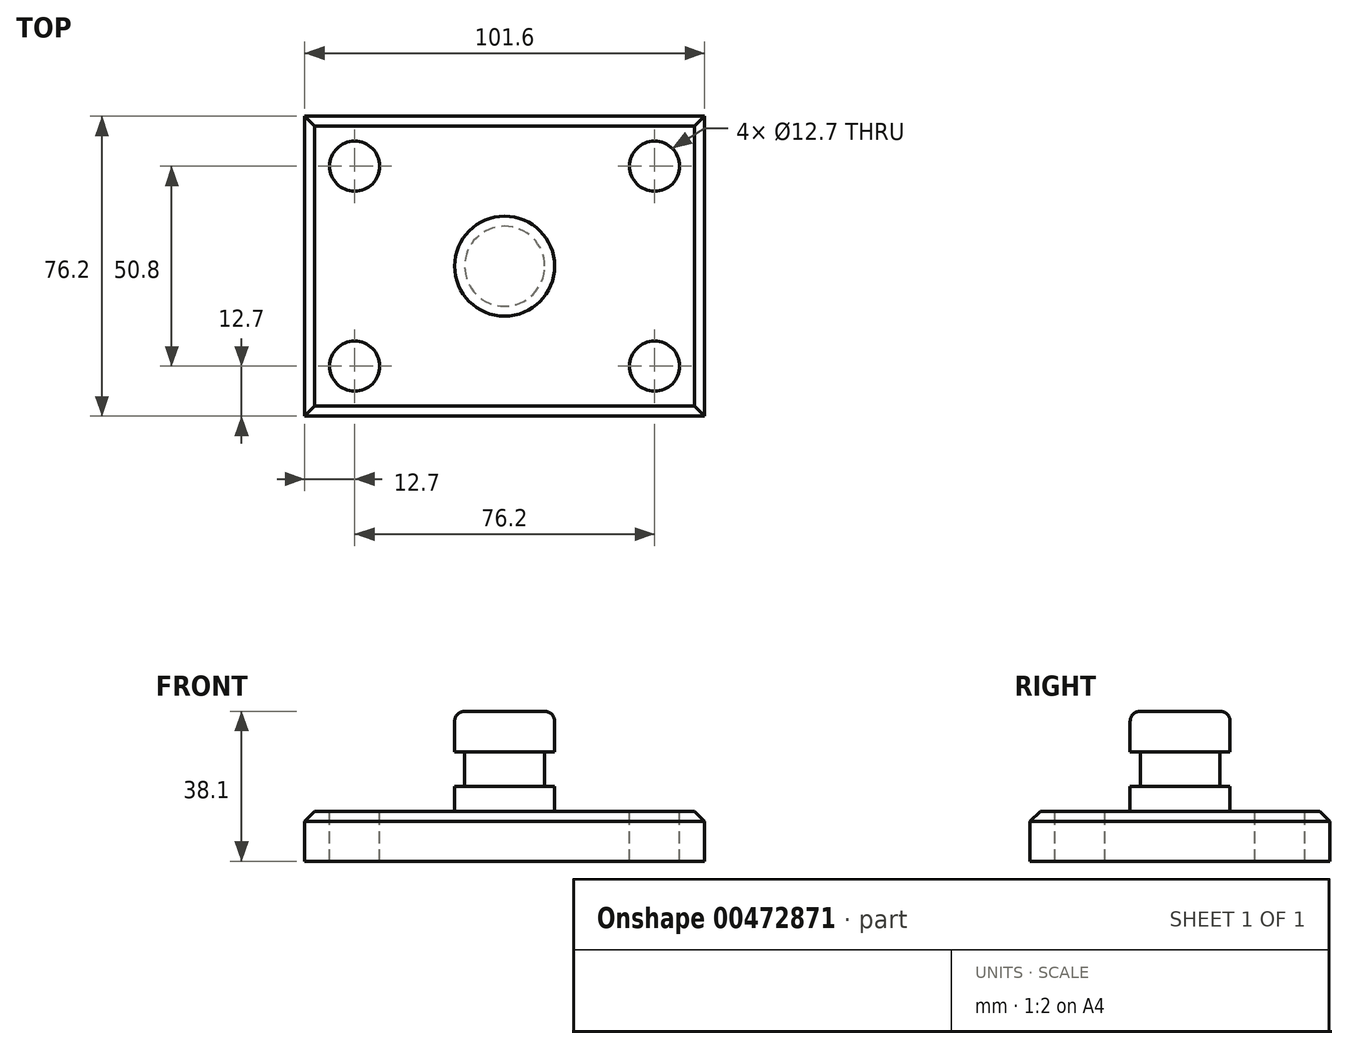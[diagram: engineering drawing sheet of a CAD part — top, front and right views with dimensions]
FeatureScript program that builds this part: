
annotation { "Feature Type Name" : "Feature", "Feature Type Description" : "" }
export const myFeature = defineFeature(function(context is Context, id is Id, definition is map)
    precondition{}
    {
        {
            var Q0;
            Q0=qCreatedBy(makeId("Top.planeOp"),FACE);
            var sketch = newSketch(context, id + "F0", { "sketchPlane" : qUnion([Q0])});
            skLineSegment(sketch, "E0.bottom", {"start": v(50.8, 38.1) * mm, "end": v(-50.8, 38.1) * mm});
            skLineSegment(sketch, "E0.top", {"start": v(50.8, -38.1) * mm, "end": v(-50.8, -38.1) * mm});
            skLineSegment(sketch, "E0.left", {"start": v(50.8, 38.1) * mm, "end": v(50.8, -38.1) * mm});
            skLineSegment(sketch, "E0.right", {"start": v(-50.8, 38.1) * mm, "end": v(-50.8, -38.1) * mm});
            skPoint(sketch, "E0.middle", {"position": v(0, 0) * mm});
            skSolve(sketch);
        }
        {
            var Q0;
            Q0=makeQuery(id+"F0.imprint","IMPRINT",FACE,{"disambiguationData":[TD([[makeQuery(id+"F0.imprint","IMPRINT",EDGE,{"derivedFrom":sQuery(id+"F0.wireOp",EDGE,"E0.bottom")}),1.0]])]});
            extrude(context, id + "F1", {"entities" : qUnion([Q0]), "depth" : 12.7 * mm});
        }
        {
            var Q0;
            Q0=makeQuery(id+"F1.opExtrude","CAP_FACE",FACE,{"disambiguationData":[OSD([sQuery(id+"F0.wireOp",EDGE,"E0.bottom"),sQuery(id+"F0.wireOp",EDGE,"E0.top"),sQuery(id+"F0.wireOp",EDGE,"E0.left"),sQuery(id+"F0.wireOp",EDGE,"E0.right")])],"isStart":false});
            var sketch = newSketch(context, id + "F2", { "sketchPlane" : qUnion([Q0])});
            skCircle(sketch, "E1", {"center": v(-38.1, 25.4) * mm, "radius": 6.35 * mm});
            skCircle(sketch, "E2", {"center": v(38.1, 25.4) * mm, "radius": 6.35 * mm});
            skCircle(sketch, "E3", {"center": v(-38.1, -25.4) * mm, "radius": 6.35 * mm});
            skCircle(sketch, "E4", {"center": v(38.1, -25.4) * mm, "radius": 6.35 * mm});
            skSolve(sketch);
        }
        {
            var Q0;
            Q0=makeQuery(id+"F2.imprint","IMPRINT",FACE,{"disambiguationData":[TD([[makeQuery(id+"F2.imprint","IMPRINT",EDGE,{"derivedFrom":sQuery(id+"F2.wireOp",EDGE,"E1")}),1.0]])]});
            var Q1;
            Q1=makeQuery(id+"F2.imprint","IMPRINT",FACE,{"disambiguationData":[TD([[makeQuery(id+"F2.imprint","IMPRINT",EDGE,{"derivedFrom":sQuery(id+"F2.wireOp",EDGE,"E2")}),1.0]])]});
            var Q2;
            Q2=makeQuery(id+"F2.imprint","IMPRINT",FACE,{"disambiguationData":[TD([[makeQuery(id+"F2.imprint","IMPRINT",EDGE,{"derivedFrom":sQuery(id+"F2.wireOp",EDGE,"E4")}),1.0]])]});
            var Q3;
            Q3=makeQuery(id+"F2.imprint","IMPRINT",FACE,{"disambiguationData":[TD([[makeQuery(id+"F2.imprint","IMPRINT",EDGE,{"derivedFrom":sQuery(id+"F2.wireOp",EDGE,"E3")}),1.0]])]});
            extrude(context, id + "F3", {"entities" : qUnion([Q0, Q1, Q2, Q3]), "operationType" : NewBodyOperationType.REMOVE, "endBound" : BoundingType.THROUGH_ALL, "oppositeDirection" : true, "depth" : 25.4 * mm});
        }
        {
            var Q0;
            Q0=qCreatedBy(makeId("Front.planeOp"),FACE);
            var sketch = newSketch(context, id + "F4", { "sketchPlane" : qUnion([Q0])});
            skLineSegment(sketch, "E5.bottom", {"start": v(0, 12.7) * mm, "end": v(12.7, 12.7) * mm});
            skLineSegment(sketch, "E5.top", {"start": v(0, 38.1) * mm, "end": v(12.7, 38.1) * mm});
            skLineSegment(sketch, "E5.left", {"start": v(0, 12.7) * mm, "end": v(0, 38.1) * mm});
            skLineSegment(sketch, "E5.right", {"start": v(12.7, 12.7) * mm, "end": v(12.7, 38.1) * mm});
            skSolve(sketch);
        }
        {
            var Q0;
            Q0=makeQuery(id+"F4.imprint","IMPRINT",FACE,{"disambiguationData":[TD([[makeQuery(id+"F4.imprint","IMPRINT",EDGE,{"derivedFrom":sQuery(id+"F4.wireOp",EDGE,"E5.bottom")}),1.0]])]});
            var Q1;
            Q1=sQuery(id+"F4.wireOp",EDGE,"E5.left");
            revolve(context, id + "F5", {"operationType" : NewBodyOperationType.ADD, "entities" : qUnion([Q0]), "axis" : qUnion([Q1]), "revolveType" : RevolveType.FULL});
        }
        {
            var Q0;
            Q0=qCreatedBy(makeId("Front.planeOp"),FACE);
            var sketch = newSketch(context, id + "F6", { "sketchPlane" : qUnion([Q0])});
            skLineSegment(sketch, "E6.bottom", {"start": v(10.16, 27.82) * mm, "end": v(18.9, 27.82) * mm});
            skLineSegment(sketch, "E6.top", {"start": v(10.16, 19.05) * mm, "end": v(18.9, 19.05) * mm});
            skLineSegment(sketch, "E6.left", {"start": v(10.16, 27.82) * mm, "end": v(10.16, 19.05) * mm});
            skLineSegment(sketch, "E6.right", {"start": v(18.9, 27.82) * mm, "end": v(18.9, 19.05) * mm});
            skSolve(sketch);
        }
        {
            var Q0;
            Q0=makeQuery(id+"F6.imprint","IMPRINT",FACE,{"disambiguationData":[TD([[makeQuery(id+"F6.imprint","IMPRINT",EDGE,{"derivedFrom":sQuery(id+"F6.wireOp",EDGE,"E6.bottom")}),-1.0]])]});
            var Q1;
            Q1=makeQuery(id+"F5.opRevolve","SWEPT_FACE",FACE,{"disambiguationData":[OSD([sQuery(id+"F4.wireOp",EDGE,"E5.right")])]});
            revolve(context, id + "F7", {"operationType" : NewBodyOperationType.REMOVE, "entities" : qUnion([Q0]), "axis" : qUnion([Q1]), "revolveType" : RevolveType.FULL, "oppositeDirection" : true});
        }
        {
            var Q0;
            Q0=makeQuery(id+"F5.opRevolve","SWEPT_EDGE",EDGE,{"disambiguationData":[OSD([sQuery(id+"F4.wireOp",EDGE,"E5.bottom"),sQuery(id+"F4.wireOp",EDGE,"E5.right")])]});
            var Q1;
            Q1=makeQuery(id+"F5.opRevolve","SWEPT_EDGE",EDGE,{"disambiguationData":[OSD([sQuery(id+"F4.wireOp",EDGE,"E5.top"),sQuery(id+"F4.wireOp",EDGE,"E5.right")])]});
            fillet(context, id + "F8", {"entities" : qUnion([Q0, Q1]), "radius" : 2.54 * mm, "tangentPropagation" : true, "allowEdgeOverflow" : false});
        }
        {
            var Q0;
            Q0=makeQuery(id+"F1.opExtrude","CAP_EDGE",EDGE,{"disambiguationData":[OSD([sQuery(id+"F0.wireOp",EDGE,"E0.top")])],"isStart":false});
            var Q1;
            Q1=makeQuery(id+"F1.opExtrude","CAP_EDGE",EDGE,{"disambiguationData":[OSD([sQuery(id+"F0.wireOp",EDGE,"E0.left")])],"isStart":false});
            var Q2;
            Q2=makeQuery(id+"F1.opExtrude","CAP_EDGE",EDGE,{"disambiguationData":[OSD([sQuery(id+"F0.wireOp",EDGE,"E0.bottom")])],"isStart":false});
            var Q3;
            Q3=makeQuery(id+"F1.opExtrude","CAP_EDGE",EDGE,{"disambiguationData":[OSD([sQuery(id+"F0.wireOp",EDGE,"E0.right")])],"isStart":false});
            chamfer(context, id + "F9", {"entities" : qUnion([Q0, Q1, Q2, Q3]), "width" : 2.54 * mm, "tangentPropagation" : true});
        }
    });
